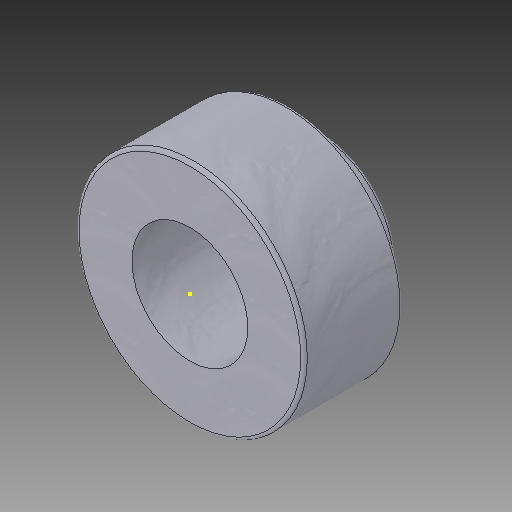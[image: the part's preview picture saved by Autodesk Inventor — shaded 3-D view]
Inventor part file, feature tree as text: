
AUTODESK INVENTOR PART (.ipt)
format: ipt  version: 2019 (Build 230136000, 136)  size: 207,360 bytes
history: native  units: in
note: dims shown in document units (in); Inventor stores cm internally (conversion verified against a paired STEP export)
features: sketch x6, other x3
ambient origin geometry x8: Origin, YZ Plane, XZ Plane, XY Plane, X Axis, Y Axis, Z Axis, Center Point
bodies: Solid1 (feature_tree)
feature tree (9):
  other  "project flange bearing part2.ipt"
  other  "Solid1::project flange bearing part2.ipt"
  other  "TaggingFeature1"
  sketch  "Sketch1"  dims[d0=0.3937in]
  sketch  "Sketch2"
  sketch  "Sketch3"
  sketch  "Sketch4"
  sketch  "Sketch5"
  sketch  "Sketch6"
